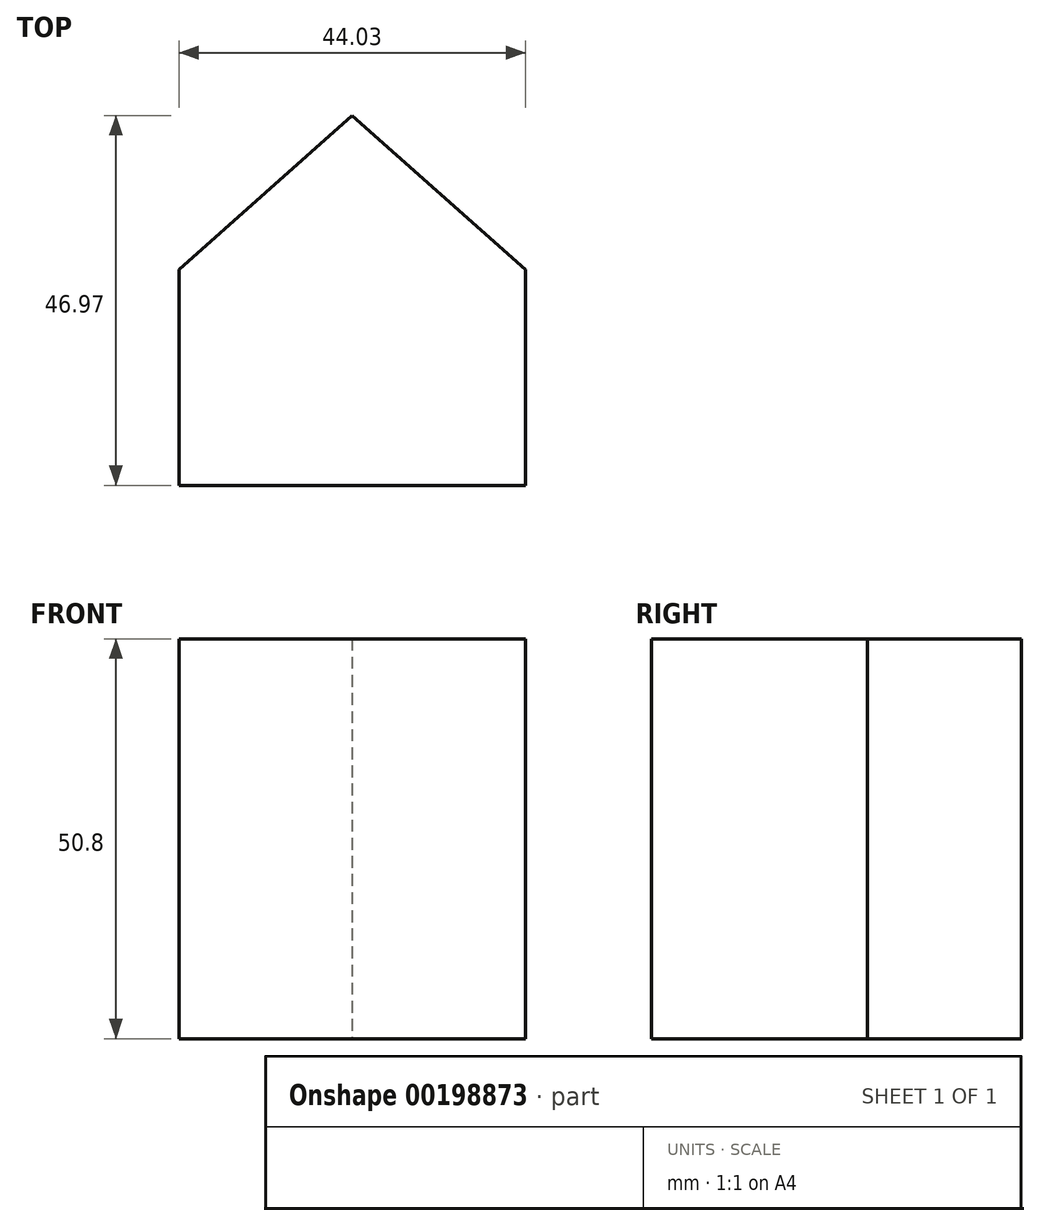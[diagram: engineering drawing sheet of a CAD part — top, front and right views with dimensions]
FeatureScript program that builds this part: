
annotation { "Feature Type Name" : "Feature", "Feature Type Description" : "" }
export const myFeature = defineFeature(function(context is Context, id is Id, definition is map)
    precondition{}
    {
        {
            var Q0;
            Q0=qCreatedBy(makeId("Top.planeOp"),FACE);
            var sketch = newSketch(context, id + "F0", { "sketchPlane" : qUnion([Q0])});
            skLineSegment(sketch, "E0", {"start": v(0, 0) * mm, "end": v(0, 27.43) * mm});
            skLineSegment(sketch, "E1", {"start": v(0, 27.43) * mm, "end": v(44.03, 27.43) * mm});
            skLineSegment(sketch, "E2", {"start": v(44.03, 27.43) * mm, "end": v(44.03, 0) * mm});
            skLineSegment(sketch, "E3", {"start": v(44.03, 0) * mm, "end": v(0, 0) * mm});
            skLineSegment(sketch, "E4", {"start": v(0, 27.43) * mm, "end": v(22.02, 46.97) * mm});
            skPoint(sketch, "E4.endSnap0", {"position": v(22.02, 27.43) * mm});
            skLineSegment(sketch, "E5", {"start": v(22.02, 46.97) * mm, "end": v(44.03, 27.43) * mm});
            skSolve(sketch);
        }
        {
            var Q0;
            Q0=makeQuery(id+"F0.imprint","IMPRINT",FACE,{"disambiguationData":[TD([[makeQuery(id+"F0.imprint","IMPRINT",EDGE,{"derivedFrom":sQuery(id+"F0.wireOp",EDGE,"E0")}),-1.0]])]});
            extrude(context, id + "F1", {"entities" : qUnion([Q0]), "depth" : 50.8 * mm});
        }
        {
            var Q0;
            Q0=makeQuery(id+"F0.imprint","IMPRINT",FACE,{"disambiguationData":[TD([[makeQuery(id+"F0.imprint","IMPRINT",EDGE,{"derivedFrom":sQuery(id+"F0.wireOp",EDGE,"E1")}),1.0]])]});
            extrude(context, id + "F2", {"entities" : qUnion([Q0]), "operationType" : NewBodyOperationType.ADD, "depth" : 50.8 * mm});
        }
    });
